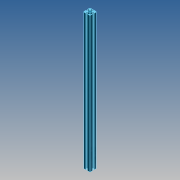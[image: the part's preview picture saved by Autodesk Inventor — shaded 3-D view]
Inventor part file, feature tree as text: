
AUTODESK INVENTOR PART (.ipt)
format: ipt  version: 2015 SP1 (Build 190203100, 203)  size: 408,576 bytes
history: native  units: mm
features: fillet x8, sketch x4, extrude x3, projected_geometry x2, mirror x1, pattern_circular x1, hole x1
ambient origin geometry x8: Origin, YZ Plane, XZ Plane, XY Plane, X Axis, Y Axis, Z Axis, Center Point
bodies: Solid1 (feature_tree)
feature tree (20):
  extrude  "Corps"  TaperAngle=45.0deg  [1 undecoded]
  extrude  "Creux"  Depth=1.5mm
  fillet  "Fillet8"  Radius=4.0mm
  fillet  "Fillet1"  Radius=2.0mm
  fillet  "Fillet2"  Radius=4.3mm
  fillet  "Fillet3"  Radius=2.0mm
  fillet  "Fillet4"  Radius=10.0mm
  fillet  "Fillet5"  Radius=6.5mm
  mirror  "Mirror1"
  fillet  "Fillet6"  Radius=7.5mm
  fillet  "Fillet7"  Radius=300.0mm
  pattern_circular  "Circular Pattern1"  [2 undecoded]
  hole  "Hole1"  [1 undecoded]
  extrude  "Extrusion4"  Depth=0.5mm
  sketch  "Sketch1"  dims[d0=20.0mm d1=45.0deg]
  sketch  "Sketch2"  dims[d2=800.0mm d3=0.0mm d4=1.5mm d5=4.0mm d6=2.0mm d7=4.3mm d8=2.0mm d9=10.0mm d10=6.5mm d12=7.5mm d13=300.0mm d14=0.0mm]
  sketch  "Sketch3"  dims[d15=3.0mm]
  sketch  "Sketch4"  dims[d16=1.0mm d17=2.0mm d18=0.5mm d19=0.5mm d20=3.0mm d21=1.0mm d22=40.0mm d23=360.0deg d25=6.0mm d26=6.0mm d27=4.0mm d28=2.0mm d29=90.0deg d30=8.0mm d31=20.594885mm d32=1.0mm d35=800.0mm d36=0.0mm]
  projected_geometry  "Project Cut Edges1"
  projected_geometry  "Project Cut Edges2"
note: 4 required parameter values undecoded (feature->parameter linkage not recoverable at this tier; creation-order binding heuristic only, values carry confidence <= 0.55)
